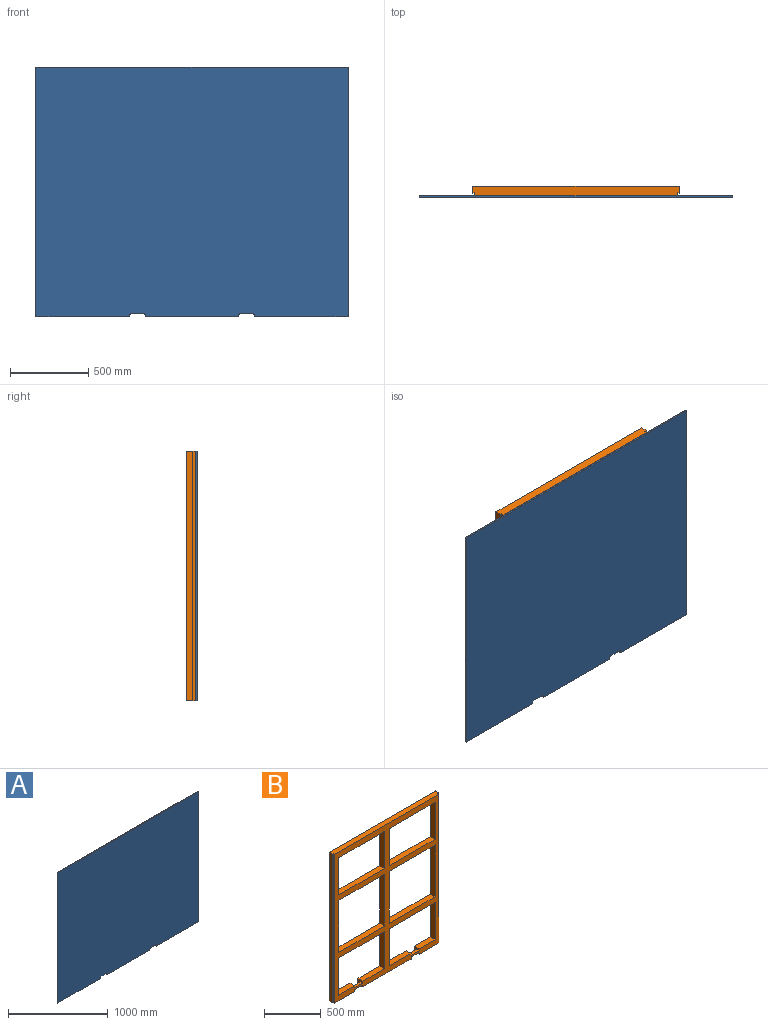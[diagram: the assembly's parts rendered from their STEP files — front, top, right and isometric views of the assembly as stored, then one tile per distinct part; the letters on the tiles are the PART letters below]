
ASSEMBLY  parts=2 mates=1
PART A: 18 faces, bbox 2000x10x1600 mm
  f0: plane 600x10mm, normal (0,0,-1), area 6000mm2, adj f5,f6,f7,f17
  f1: plane 600x10mm, normal (0,0,-1), area 6000mm2, adj f6,f7,f12,f13
  f2: plane 600x10mm, normal (0,0,-1), area 6000mm2, adj f3,f6,f7,f8
  f3: plane 1600x10mm, normal (1,0,0), area 16000mm2, adj f2,f4,f6,f7
  f4: plane 2000x10mm, normal (0,0,1), area 20000mm2, adj f3,f5,f6,f7
  f5: plane 1600x10mm, normal (-1,0,0), area 16000mm2, adj f0,f4,f6,f7
  f6: plane 2000x1600mm, normal (0,-1,0), area 3196085.8mm2, adj f0,f1,f2,f3,f4,f5,f8,f9
  f7: plane 2000x1600mm, normal (0,1,0), area 3196085.8mm2, adj f0,f1,f2,f3,f4,f5,f8,f9
  f8: plane 10x10mm, normal (-1,0,0), area 100mm2, adj f2,f6,f7,f9
  f9: cylinder r=10mm len=10mm, axis (0,-1,0), area 157.1mm2, adj f6,f7,f8,f10
  f10: plane 80x10mm, normal (0,0,-1), area 800mm2, adj f6,f7,f9,f11
  f11: cylinder r=10mm len=10mm, axis (0,-1,0), area 157.1mm2, adj f6,f7,f10,f12
  f12: plane 10x10mm, normal (1,0,0), area 100mm2, adj f1,f6,f7,f11
  f13: plane 10x10mm, normal (-1,0,0), area 100mm2, adj f1,f6,f7,f14
  f14: cylinder r=10mm len=10mm, axis (0,-1,0), area 157.1mm2, adj f6,f7,f13,f15
  f15: plane 80x10mm, normal (0,0,-1), area 800mm2, adj f6,f7,f14,f16
  f16: cylinder r=10mm len=10mm, axis (0,-1,0), area 157.1mm2, adj f6,f7,f15,f17
  f17: plane 10x10mm, normal (1,0,0), area 100mm2, adj f0,f6,f7,f16
PART B: 52 faces, bbox 1320x60x1600 mm
  f0: plane 270x60mm, normal (0,0,1), area 16200mm2, adj f2,f15,f22,f46
  f1: plane 200x60mm, normal (0,0,1), area 12000mm2, adj f2,f15,f27,f44
  f2: plane 1600x1320mm, normal (0,1,0), area 549600mm2, adj f0,f1,f9,f10,f11,f12,f13,f14
  f3: cylinder r=10mm len=30mm, axis (0,-1,0), area 471.2mm2, adj f4,f15,f44,f49
  f4: plane 80x30mm, normal (0,0,-1), area 2400mm2, adj f3,f5,f15,f49
  f5: cylinder r=10mm len=30mm, axis (0,-1,0), area 471.2mm2, adj f4,f15,f45,f49
  f6: cylinder r=10mm len=30mm, axis (0,-1,0), area 471.2mm2, adj f7,f15,f46,f48
  f7: plane 80x30mm, normal (0,0,-1), area 2400mm2, adj f6,f8,f15,f48
  f8: cylinder r=10mm len=30mm, axis (0,-1,0), area 471.2mm2, adj f7,f15,f47,f48
  f9: plane 260x60mm, normal (0,0,-1), area 15372mm2, adj f2,f13,f15,f42,f43,f47
  f10: plane 600x60mm, normal (0,0,-1), area 36000mm2, adj f2,f15,f45,f46
  f11: plane 1600x41mm, normal (1,0,0), area 65600mm2, adj f2,f12,f14,f41
  f12: plane 1320x60mm, normal (0,0,1), area 78744mm2, adj f2,f11,f13,f15,f40,f41,f42,f43
  f13: plane 1600x41mm, normal (-1,0,0), area 65600mm2, adj f2,f9,f12,f43
  f14: plane 260x60mm, normal (0,0,-1), area 15372mm2, adj f2,f11,f15,f40,f41,f44
  f15: plane 1600x1296mm, normal (0,-1,0), area 515285.8mm2, adj f0,f1,f3,f4,f5,f6,f7,f8
  f16: plane 570x60mm, normal (0,0,1), area 34200mm2, adj f2,f15,f17,f39
  f17: plane 560x60mm, normal (1,0,0), area 33600mm2, adj f2,f15,f16,f18
  f18: plane 570x60mm, normal (0,0,-1), area 34200mm2, adj f2,f15,f17,f39
  f19: plane 570x60mm, normal (0,0,1), area 34200mm2, adj f2,f15,f20,f34
  f20: plane 400x60mm, normal (1,0,0), area 24000mm2, adj f2,f15,f19,f21
  f21: plane 570x60mm, normal (0,0,-1), area 34200mm2, adj f2,f15,f20,f34
  f22: plane 400x60mm, normal (-1,0,0), area 24000mm2, adj f0,f2,f15,f35
  f23: plane 200x60mm, normal (0,0,1), area 12000mm2, adj f2,f15,f24,f47
  f24: plane 400x60mm, normal (1,0,0), area 24000mm2, adj f2,f15,f23,f35
  f25: plane 400x60mm, normal (1,0,0), area 24000mm2, adj f2,f15,f26,f36
  f26: plane 570x60mm, normal (0,0,-1), area 34200mm2, adj f2,f15,f25,f27
  f27: plane 400x60mm, normal (-1,0,0), area 24000mm2, adj f1,f2,f15,f26
  f28: plane 400x60mm, normal (-1,0,0), area 24000mm2, adj f2,f15,f29,f37
  f29: plane 570x60mm, normal (0,0,1), area 34200mm2, adj f2,f15,f28,f30
  f30: plane 400x60mm, normal (1,0,0), area 24000mm2, adj f2,f15,f29,f37
  f31: plane 560x60mm, normal (-1,0,0), area 33600mm2, adj f2,f15,f32,f38
  f32: plane 570x60mm, normal (0,0,1), area 34200mm2, adj f2,f15,f31,f33
  f33: plane 560x60mm, normal (1,0,0), area 33600mm2, adj f2,f15,f32,f38
  f34: plane 400x60mm, normal (-1,0,0), area 24000mm2, adj f2,f15,f19,f21
  f35: plane 570x60mm, normal (0,0,-1), area 34200mm2, adj f2,f15,f22,f24
  f36: plane 270x60mm, normal (0,0,1), area 16200mm2, adj f2,f15,f25,f45
  f37: plane 570x60mm, normal (0,0,-1), area 34200mm2, adj f2,f15,f28,f30
  f38: plane 570x60mm, normal (0,0,-1), area 34200mm2, adj f2,f15,f31,f33
  f39: plane 560x60mm, normal (-1,0,0), area 33600mm2, adj f2,f15,f16,f18
  f40: plane 1600x19mm, normal (1,0,0), area 30400mm2, adj f12,f14,f15,f41
  f41: plane 1600x12mm, normal (0,-1,0), area 19200mm2, adj f11,f12,f14,f40
  f42: plane 1600x19mm, normal (-1,0,0), area 30400mm2, adj f9,f12,f15,f43
  f43: plane 1600x12mm, normal (0,-1,0), area 19200mm2, adj f9,f12,f13,f42
  f44: plane 60x60mm, normal (-1,0,0), area 2700mm2, adj f1,f2,f3,f14,f15,f49,f50
  f45: plane 60x60mm, normal (1,0,0), area 2700mm2, adj f2,f5,f10,f15,f36,f49,f50
  f46: plane 60x60mm, normal (-1,0,0), area 2700mm2, adj f0,f2,f6,f10,f15,f48,f51
  f47: plane 60x60mm, normal (1,0,0), area 2700mm2, adj f2,f8,f9,f15,f23,f48,f51
  f48: plane 100x30mm, normal (0,1,0), area 2042.9mm2, adj f6,f7,f8,f46,f47,f51
  f49: plane 100x30mm, normal (0,1,0), area 2042.9mm2, adj f3,f4,f5,f44,f45,f50
  f50: plane 100x30mm, normal (0,0,1), area 3000mm2, adj f15,f44,f45,f49
  f51: plane 100x30mm, normal (0,0,1), area 3000mm2, adj f15,f46,f47,f48
PLACE A t=(667.71,437.16,77.84)mm
PLACE B t=(667.71,497.16,77.84)mm
MATE fastened B.f12 <-> A.f4  axis (0,0,1) through (1315.71,437.16,877.84)mm
